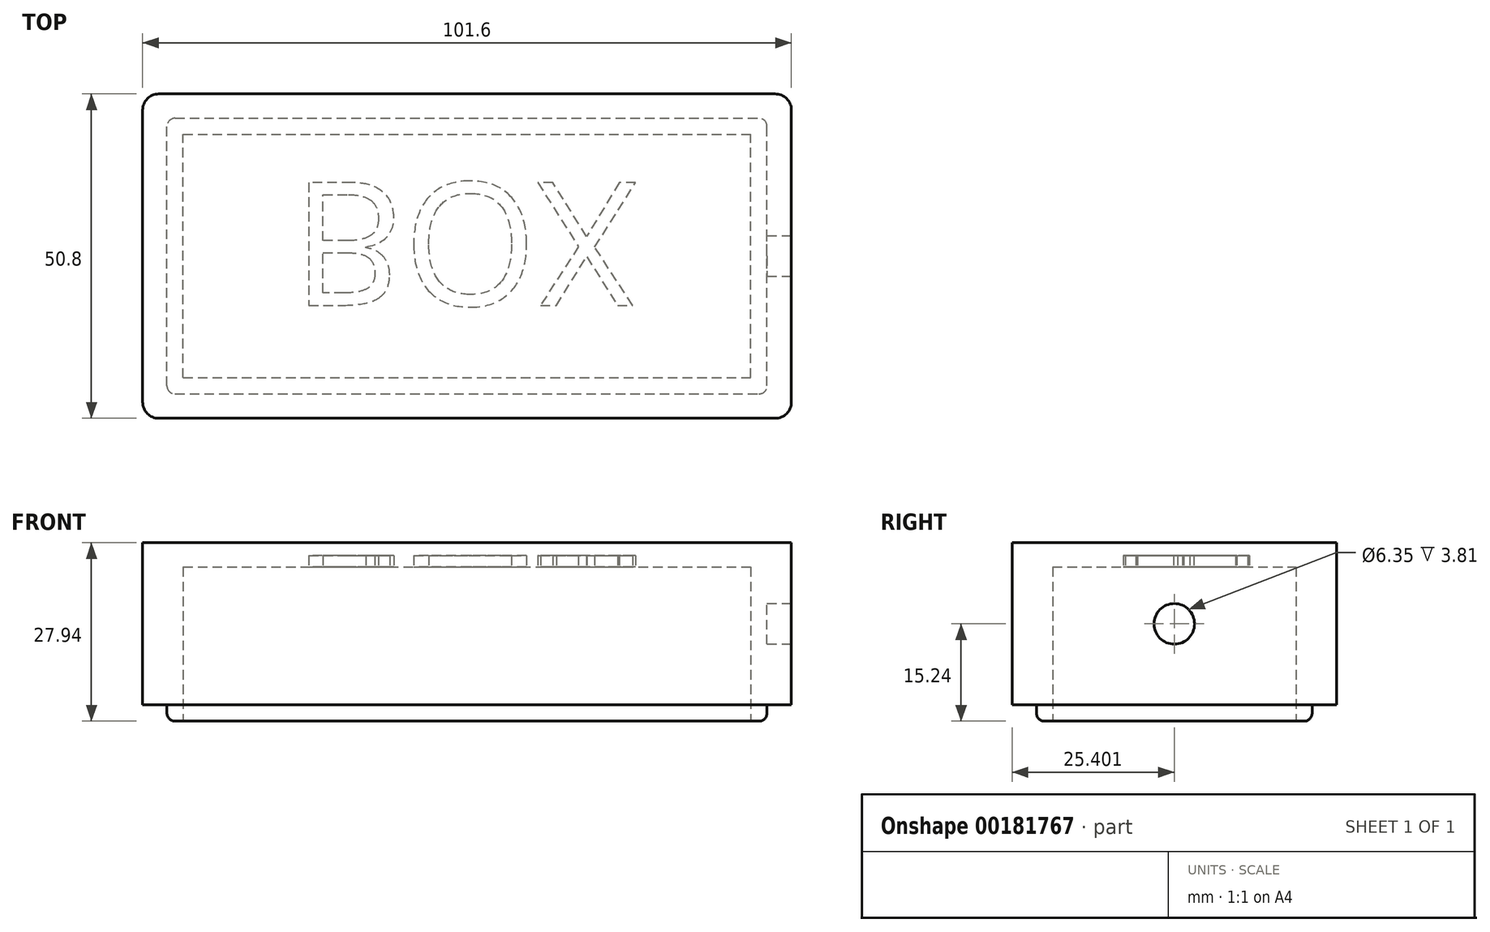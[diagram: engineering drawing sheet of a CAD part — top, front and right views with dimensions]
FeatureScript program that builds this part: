
annotation { "Feature Type Name" : "Feature", "Feature Type Description" : "" }
export const myFeature = defineFeature(function(context is Context, id is Id, definition is map)
    precondition{}
    {
        {
            var Q0;
            Q0=qCreatedBy(makeId("Top.planeOp"),FACE);
            var sketch = newSketch(context, id + "F0", { "sketchPlane" : qUnion([Q0])});
            skLineSegment(sketch, "E0.bottom", {"start": v(-76.27, -25.76) * mm, "end": v(25.33, -25.76) * mm});
            skLineSegment(sketch, "E0.top", {"start": v(-76.27, 25.04) * mm, "end": v(25.33, 25.04) * mm});
            skLineSegment(sketch, "E0.left", {"start": v(-76.27, -25.76) * mm, "end": v(-76.27, 25.04) * mm});
            skLineSegment(sketch, "E0.right", {"start": v(25.33, -25.76) * mm, "end": v(25.33, 25.04) * mm});
            skSolve(sketch);
        }
        {
            var Q0;
            Q0=makeQuery(id+"F0.imprint","IMPRINT",FACE,{"disambiguationData":[TD([[makeQuery(id+"F0.imprint","IMPRINT",EDGE,{"derivedFrom":sQuery(id+"F0.wireOp",EDGE,"E0.bottom")}),1.0]])]});
            extrude(context, id + "F1", {"entities" : qUnion([Q0]), "depth" : 25.4 * mm});
        }
        {
            var Q0;
            Q0=makeQuery(id+"F1.opExtrude","CAP_FACE",FACE,{"disambiguationData":[OSD([sQuery(id+"F0.wireOp",EDGE,"E0.bottom"),sQuery(id+"F0.wireOp",EDGE,"E0.top"),sQuery(id+"F0.wireOp",EDGE,"E0.left"),sQuery(id+"F0.wireOp",EDGE,"E0.right")])],"isStart":true});
            shell(context, id + "F2", {"entities" : qUnion([Q0]), "thickness" : 3.8 * mm});
        }
        {
            var Q0;
            Q0=makeQuery(id+"F1.opExtrude","SWEPT_FACE",FACE,{"disambiguationData":[OSD([sQuery(id+"F0.wireOp",EDGE,"E0.right")])]});
            var sketch = newSketch(context, id + "F3", { "sketchPlane" : qUnion([Q0])});
            skPoint(sketch, "E1", {"position": v(-0.36, 12.7) * mm});
            skSolve(sketch);
        }
        {
            var Q0;
            Q0=sQuery(id+"F3.wireOp",VERTEX,"E1");
            var Q1;
            Q1=makeQuery(id+"F1.opExtrude","SWEPT_BODY",BODY,{"disambiguationData":[OSD([sQuery(id+"F0.wireOp",EDGE,"E0.bottom"),sQuery(id+"F0.wireOp",EDGE,"E0.top"),sQuery(id+"F0.wireOp",EDGE,"E0.left"),sQuery(id+"F0.wireOp",EDGE,"E0.right")])]});
            hole(context, id + "F4", {"style" : HoleStyle.SIMPLE, "endStyle" : HoleEndStyle.BLIND, "holeDiameter" : 6.35 * mm, "holeDepth" : 12.7 * mm, "locations" : qUnion([Q0]), "scope" : qUnion([Q1])});
        }
        {
            var Q0;
            Q0=makeQuery(id+"F2.opShell","OFFSET_FACE",FACE,{"disambiguationData":[OSD([sQuery(id+"F0.wireOp",EDGE,"E0.bottom"),sQuery(id+"F0.wireOp",EDGE,"E0.top"),sQuery(id+"F0.wireOp",EDGE,"E0.left"),sQuery(id+"F0.wireOp",EDGE,"E0.right")])]});
            var sketch = newSketch(context, id + "F5", { "sketchPlane" : qUnion([Q0])});
            skText(sketch, "E2", { "text": "BOX", "fontName": "OpenSans-Regular.ttf"});
            const initialGuessF5  = {"E2": [-0.0529, -0.01116, 1, 0, 0.01938]};
            skSetInitialGuess(sketch, initialGuessF5);
            skSolve(sketch);
        }
        {
            var Q0;
            Q0 = qSketchRegion(id + "F5", true);
            extrude(context, id + "F6", {"entities" : qUnion([Q0]), "operationType" : NewBodyOperationType.REMOVE, "oppositeDirection" : true, "depth" : 1.78 * mm});
        }
        {
            var Q0;
            Q0=makeQuery(id+"F1.opExtrude","CAP_FACE",FACE,{"disambiguationData":[OSD([sQuery(id+"F0.wireOp",EDGE,"E0.bottom"),sQuery(id+"F0.wireOp",EDGE,"E0.top"),sQuery(id+"F0.wireOp",EDGE,"E0.left"),sQuery(id+"F0.wireOp",EDGE,"E0.right")])],"isStart":true});
            var sketch = newSketch(context, id + "F7", { "sketchPlane" : qUnion([Q0])});
            skLineSegment(sketch, "E3.bottom", {"start": v(-72.46, 21.95) * mm, "end": v(21.52, 21.95) * mm});
            skLineSegment(sketch, "E3.top", {"start": v(-72.46, -21.23) * mm, "end": v(21.52, -21.23) * mm});
            skLineSegment(sketch, "E3.left", {"start": v(-72.46, 21.95) * mm, "end": v(-72.46, -21.23) * mm});
            skLineSegment(sketch, "E3.right", {"start": v(21.52, 21.95) * mm, "end": v(21.52, -21.23) * mm});
            skLineSegment(sketch, "E4.bottom", {"start": v(-69.92, 19.4) * mm, "end": v(18.98, 19.4) * mm});
            skLineSegment(sketch, "E4.top", {"start": v(-69.92, -18.7) * mm, "end": v(18.98, -18.7) * mm});
            skLineSegment(sketch, "E4.left", {"start": v(-69.92, 19.4) * mm, "end": v(-69.92, -18.7) * mm});
            skLineSegment(sketch, "E4.right", {"start": v(18.98, 19.4) * mm, "end": v(18.98, -18.7) * mm});
            skSolve(sketch);
        }
        {
            var Q0;
            Q0=makeQuery(id+"F7.imprint","IMPRINT",FACE,{"disambiguationData":[TD([[makeQuery(id+"F7.imprint","IMPRINT",EDGE,{"derivedFrom":sQuery(id+"F7.wireOp",EDGE,"E3.bottom")}),-1.0]])]});
            var Q1;
            {var subQ0=sQuery(id+"F0.wireOp",EDGE,"E0.right");var subQ1=sQuery(id+"F0.wireOp",EDGE,"E0.left");var subQ2=sQuery(id+"F0.wireOp",EDGE,"E0.top");var subQ3=sQuery(id+"F0.wireOp",EDGE,"E0.bottom");Q1=makeQuery(id+"F6.boolean.opBoolean","SPLIT",FACE,{"disambiguationData":[TD([makeQuery(id+"F2.opShell","OFFSET_FACE",FACE,{"disambiguationData":[OSD([subQ3])]})])],"derivedFrom":makeQuery(id+"F2.opShell","OFFSET_FACE",FACE,{"disambiguationData":[OSD([subQ3,subQ2,subQ1,subQ0])]})});}
            extrude(context, id + "F8", {"entities" : qUnion([Q0]), "operationType" : NewBodyOperationType.ADD, "endBound" : BoundingType.UP_TO_SURFACE, "oppositeDirection" : true, "endBoundEntityFace" : qUnion([Q1]), "depth" : 25.4 * mm, "hasSecondDirection" : true, "secondDirectionOppositeDirection" : false, "secondDirectionDepth" : 2.54 * mm});
        }
        {
            var Q0;
            Q0=makeQuery(id+"F8.opExtrude","SWEPT_EDGE",EDGE,{"disambiguationData":[OSD([sQuery(id+"F7.wireOp",EDGE,"E3.bottom"),sQuery(id+"F7.wireOp",EDGE,"E3.right")])]});
            var Q1;
            Q1=makeQuery(id+"F8.opExtrude","SWEPT_EDGE",EDGE,{"disambiguationData":[OSD([sQuery(id+"F7.wireOp",EDGE,"E3.bottom"),sQuery(id+"F7.wireOp",EDGE,"E3.left")])]});
            var Q2;
            Q2=makeQuery(id+"F8.opExtrude","SWEPT_EDGE",EDGE,{"disambiguationData":[OSD([sQuery(id+"F7.wireOp",EDGE,"E3.top"),sQuery(id+"F7.wireOp",EDGE,"E3.right")])]});
            var Q3;
            Q3=makeQuery(id+"F8.opExtrude","SWEPT_EDGE",EDGE,{"disambiguationData":[OSD([sQuery(id+"F7.wireOp",EDGE,"E3.top"),sQuery(id+"F7.wireOp",EDGE,"E3.left")])]});
            var Q4;
            Q4=makeQuery(id+"F8.opExtrude","CAP_EDGE",EDGE,{"disambiguationData":[OSD([sQuery(id+"F7.wireOp",EDGE,"E3.bottom")])],"isStart":true});
            var Q5;
            Q5=makeQuery(id+"F8.opExtrude","CAP_EDGE",EDGE,{"disambiguationData":[OSD([sQuery(id+"F7.wireOp",EDGE,"E3.left")])],"isStart":true});
            var Q6;
            Q6=makeQuery(id+"F8.opExtrude","CAP_EDGE",EDGE,{"disambiguationData":[OSD([sQuery(id+"F7.wireOp",EDGE,"E3.top")])],"isStart":true});
            var Q7;
            Q7=makeQuery(id+"F8.opExtrude","CAP_EDGE",EDGE,{"disambiguationData":[OSD([sQuery(id+"F7.wireOp",EDGE,"E3.right")])],"isStart":true});
            fillet(context, id + "F9", {"entities" : qUnion([Q0, Q1, Q2, Q3, Q4, Q5, Q6, Q7]), "radius" : 1.27 * mm, "tangentPropagation" : true, "allowEdgeOverflow" : false});
        }
        {
            var Q0;
            Q0=makeQuery(id+"F1.opExtrude","SWEPT_EDGE",EDGE,{"disambiguationData":[OSD([sQuery(id+"F0.wireOp",EDGE,"E0.bottom"),sQuery(id+"F0.wireOp",EDGE,"E0.right")])]});
            fillet(context, id + "F10", {"entities" : qUnion([Q0]), "radius" : 2.54 * mm, "tangentPropagation" : true, "allowEdgeOverflow" : false});
        }
        {
            var Q0;
            Q0=makeQuery(id+"F1.opExtrude","SWEPT_EDGE",EDGE,{"disambiguationData":[OSD([sQuery(id+"F0.wireOp",EDGE,"E0.bottom"),sQuery(id+"F0.wireOp",EDGE,"E0.left")])]});
            var Q1;
            Q1=makeQuery(id+"F1.opExtrude","SWEPT_EDGE",EDGE,{"disambiguationData":[OSD([sQuery(id+"F0.wireOp",EDGE,"E0.top"),sQuery(id+"F0.wireOp",EDGE,"E0.left")])]});
            var Q2;
            Q2=makeQuery(id+"F1.opExtrude","SWEPT_EDGE",EDGE,{"disambiguationData":[OSD([sQuery(id+"F0.wireOp",EDGE,"E0.top"),sQuery(id+"F0.wireOp",EDGE,"E0.right")])]});
            fillet(context, id + "F11", {"entities" : qUnion([Q0, Q1, Q2]), "radius" : 2.54 * mm, "tangentPropagation" : true, "allowEdgeOverflow" : false});
        }
    });
